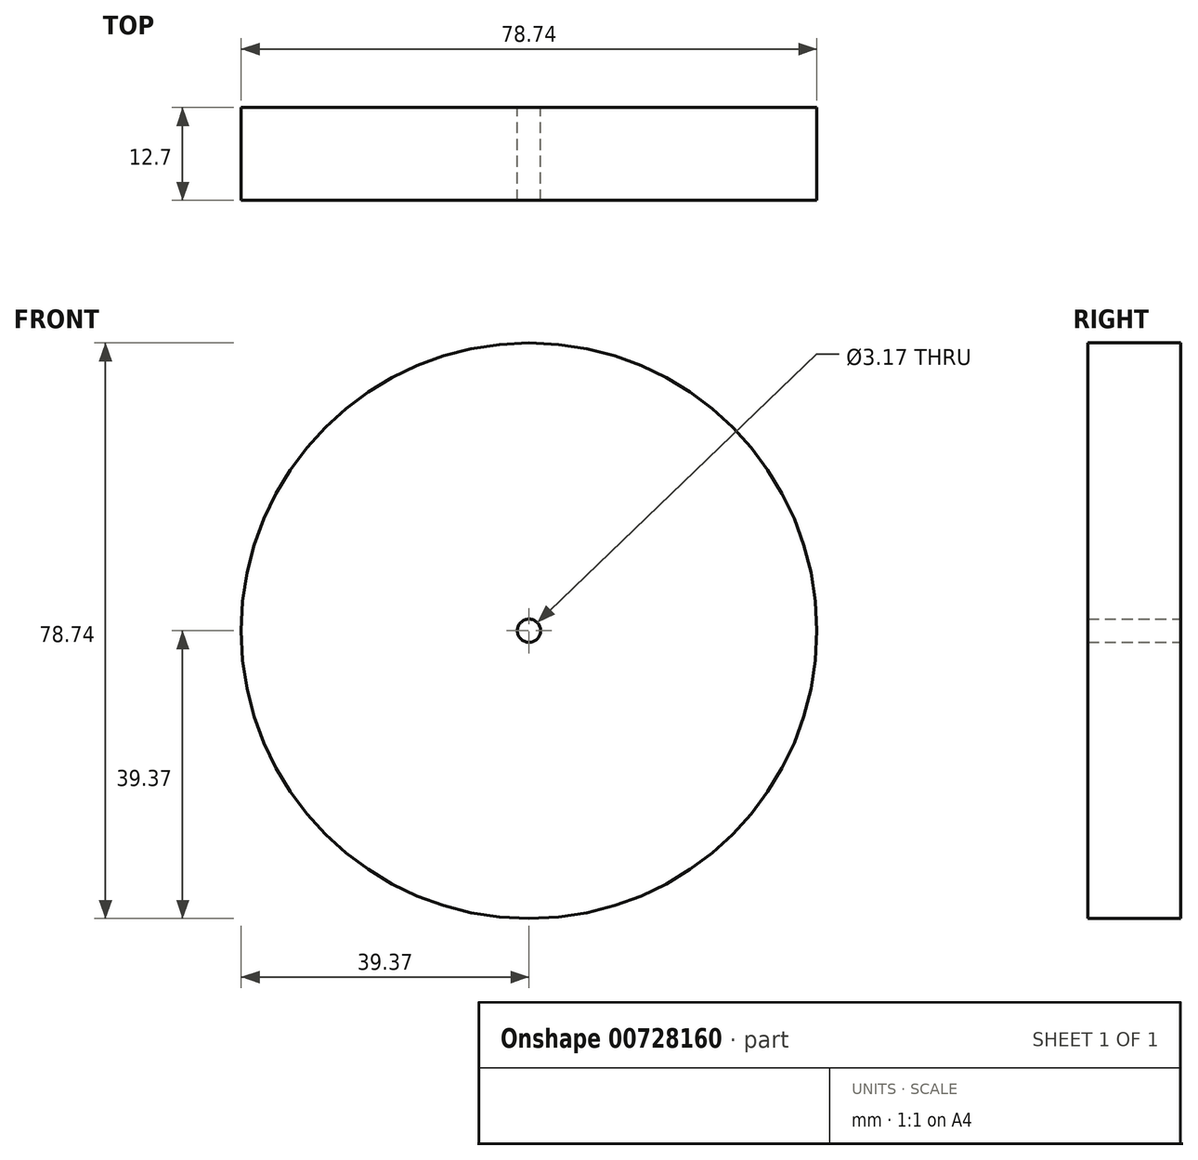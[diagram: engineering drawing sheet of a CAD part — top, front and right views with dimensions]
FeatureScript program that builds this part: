
annotation { "Feature Type Name" : "Feature", "Feature Type Description" : "" }
export const myFeature = defineFeature(function(context is Context, id is Id, definition is map)
    precondition{}
    {
        {
            var Q0;
            Q0=qCreatedBy(makeId("Front.planeOp"),FACE);
            var sketch = newSketch(context, id + "F0", { "sketchPlane" : qUnion([Q0])});
            skCircle(sketch, "E0", {"center": v(0, 0) * mm, "radius": 39.37 * mm});
            skCircle(sketch, "E1", {"center": v(0, 0) * mm, "radius": 1.59 * mm});
            skSolve(sketch);
        }
        {
            var Q0;
            Q0=makeQuery(id+"F0.imprint","IMPRINT",FACE,{"disambiguationData":[TD([[makeQuery(id+"F0.imprint","IMPRINT",EDGE,{"derivedFrom":sQuery(id+"F0.wireOp",EDGE,"E0")}),1.0]])]});
            extrude(context, id + "F1", {"entities" : qUnion([Q0]), "depth" : 12.7 * mm, "offsetDistance" : 25.4 * mm});
        }
    });
